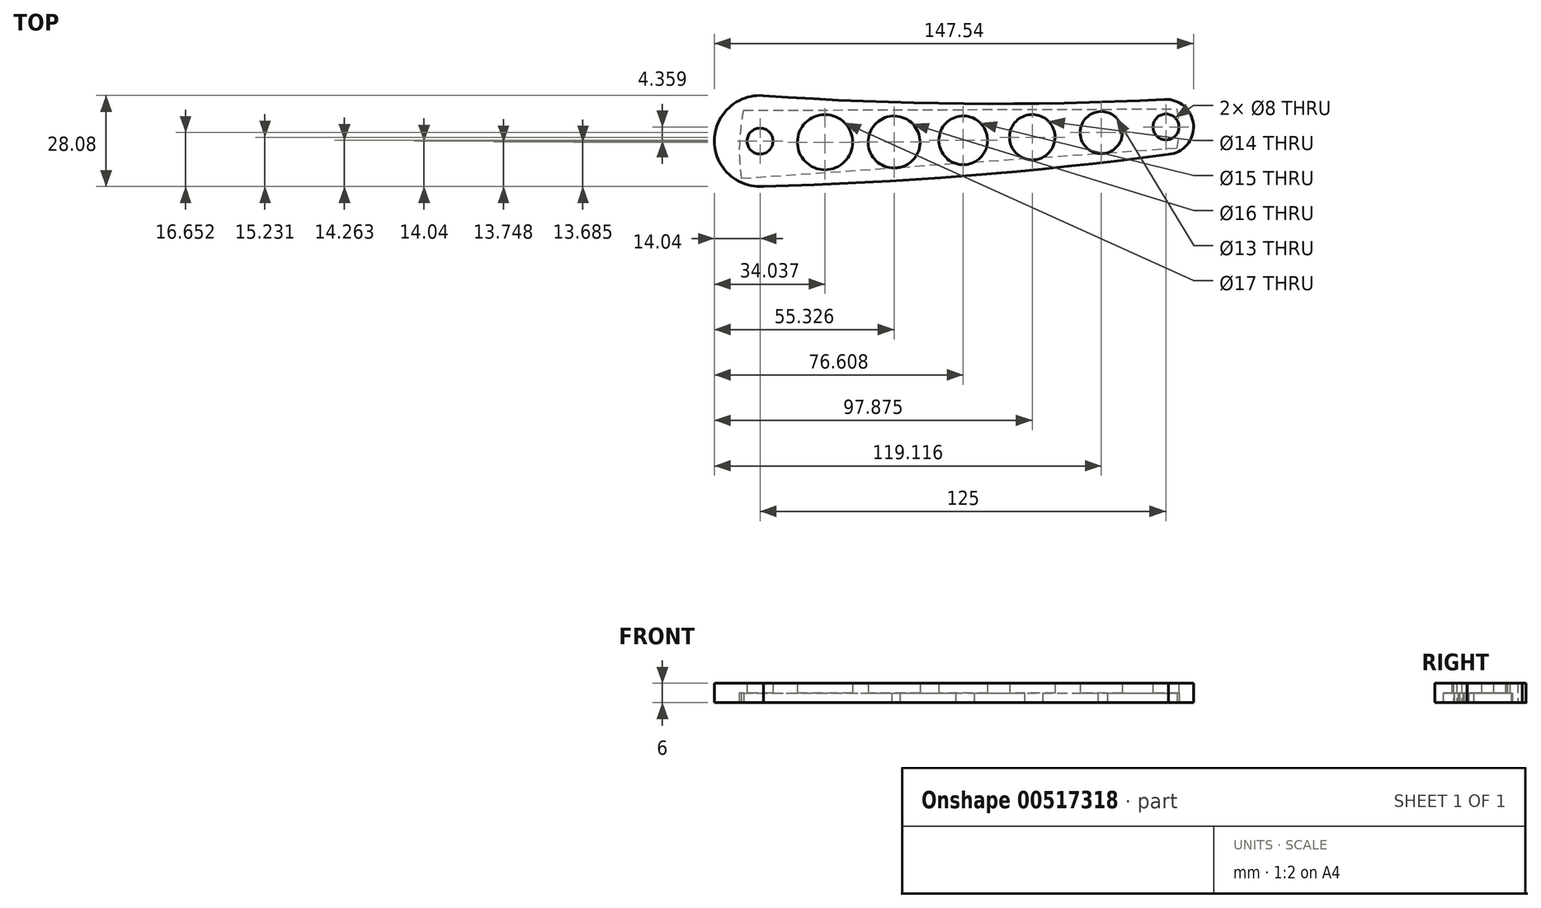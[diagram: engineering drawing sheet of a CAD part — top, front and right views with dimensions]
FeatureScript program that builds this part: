
annotation { "Feature Type Name" : "Feature", "Feature Type Description" : "" }
export const myFeature = defineFeature(function(context is Context, id is Id, definition is map)
    precondition{}
    {
        {
            var Q0;
            Q0=qCreatedBy(makeId("Top.planeOp"),FACE);
            var sketch = newSketch(context, id + "F0", { "sketchPlane" : qUnion([Q0])});
            skPoint(sketch, "E0", {"position": v(-80, 14) * mm});
            skPoint(sketch, "E1", {"position": v(45, 18.36) * mm});
            skArc(sketch, "E2", {"start": v(-79, 28) * mm, "mid": v(-17.24, 25.51) * mm, "end": v(44.55, 26.85) * mm});
            skArc(sketch, "E3", {"start": v(-80, 14) * mm, "mid": v(-17.43, 14.22) * mm, "end": v(45, 18.36) * mm, "construction": true});
            skArc(sketch, "E4", {"start": v(45.74, 9.9) * mm, "mid": v(53.48, 18.95) * mm, "end": v(44.55, 26.85) * mm});
            skArc(sketch, "E5", {"start": v(-79, 28) * mm, "mid": v(-94.04, 14) * mm, "end": v(-79, 0) * mm});
            skCircle(sketch, "E6", {"center": v(-80, 14) * mm, "radius": 4 * mm});
            skCircle(sketch, "E7", {"center": v(45, 18.36) * mm, "radius": 4 * mm});
            skCircle(sketch, "E8", {"center": v(-60, 13.65) * mm, "radius": 8.5 * mm});
            skCircle(sketch, "E9", {"center": v(-38.71, 13.7) * mm, "radius": 8 * mm});
            skCircle(sketch, "E10", {"center": v(-17.43, 14.22) * mm, "radius": 7.5 * mm});
            skCircle(sketch, "E11", {"center": v(3.84, 15.2) * mm, "radius": 7 * mm});
            skCircle(sketch, "E12", {"center": v(25.08, 16.61) * mm, "radius": 6.5 * mm});
            skLineSegment(sketch, "E13", {"start": v(-80, 14) * mm, "end": v(-60, 13.65) * mm, "construction": true});
            skLineSegment(sketch, "E14", {"start": v(-60, 13.65) * mm, "end": v(-38.71, 13.7) * mm, "construction": true});
            skLineSegment(sketch, "E15", {"start": v(-38.71, 13.7) * mm, "end": v(-17.43, 14.22) * mm, "construction": true});
            skLineSegment(sketch, "E16", {"start": v(-17.43, 14.22) * mm, "end": v(3.84, 15.2) * mm, "construction": true});
            skLineSegment(sketch, "E17", {"start": v(25.08, 16.61) * mm, "end": v(45, 18.36) * mm, "construction": true});
            skLineSegment(sketch, "E18", {"start": v(3.84, 15.2) * mm, "end": v(25.08, 16.61) * mm, "construction": true});
            skArc(sketch, "E19", {"start": v(-79, 0) * mm, "mid": v(-16.5, 3.3) * mm, "end": v(45.74, 9.9) * mm});
            skLineSegment(sketch, "E20", {"start": v(45, 18.36) * mm, "end": v(45.74, 9.9) * mm, "construction": true});
            skLineSegment(sketch, "E21", {"start": v(41.68, 9.36) * mm, "end": v(62.93, 12.1) * mm, "construction": true});
            skLineSegment(sketch, "E22", {"start": v(44.55, 26.85) * mm, "end": v(58.75, 27.6) * mm, "construction": true});
            skLineSegment(sketch, "E23", {"start": v(45, 18.36) * mm, "end": v(45, 64.58) * mm, "construction": true});
            skLineSegment(sketch, "E24", {"start": v(-79, 28) * mm, "end": v(-120.43, 30.95) * mm, "construction": true});
            skLineSegment(sketch, "E25", {"start": v(-73.81, 0.15) * mm, "end": v(-120.98, -1.31) * mm, "construction": true});
            skLineSegment(sketch, "E26", {"start": v(73.87, 0) * mm, "end": v(-126.58, 0) * mm, "construction": true});
            skSolve(sketch);
        }
        {
            var Q0;
            Q0 = qSketchRegion(id + "F0", true);
            extrude(context, id + "F1", {"entities" : qUnion([Q0]), "depth" : 6 * mm, "offsetDistance" : 25 * mm});
        }
        {
            var Q0;
            Q0=qCreatedBy(makeId("Top.planeOp"),FACE);
            var sketch = newSketch(context, id + "F2", { "sketchPlane" : qUnion([Q0])});
            skLineSegment(sketch, "E27", {"start": v(-85.1, 23.49) * mm, "end": v(48.4, 23.88) * mm});
            skLineSegment(sketch, "E28", {"start": v(48.4, 23.88) * mm, "end": v(48.44, 11.88) * mm, "construction": true});
            skLineSegment(sketch, "E29", {"start": v(-85.1, 23.49) * mm, "end": v(-85.77, 2.5) * mm, "construction": true});
            skLineSegment(sketch, "E30", {"start": v(-85.77, 2.5) * mm, "end": v(48.44, 11.88) * mm});
            skArc(sketch, "E31", {"start": v(48.44, 11.88) * mm, "mid": v(49.1, 17.89) * mm, "end": v(48.4, 23.88) * mm});
            skArc(sketch, "E32", {"start": v(-85.1, 23.49) * mm, "mid": v(-86.36, 13.02) * mm, "end": v(-85.77, 2.5) * mm});
            skLineSegment(sketch, "E33", {"start": v(45, -4.12) * mm, "end": v(45, 30.95) * mm, "construction": true});
            skLineSegment(sketch, "E34", {"start": v(-70.34, 2.5) * mm, "end": v(-85.77, 2.5) * mm, "construction": true});
            skPoint(sketch, "E35", {"position": v(45, 18.36) * mm});
            skLineSegment(sketch, "E36", {"start": v(-80, 14) * mm, "end": v(-85.1, 23.49) * mm, "construction": true});
            skLineSegment(sketch, "E37", {"start": v(-80, 14) * mm, "end": v(-91.7, 14.37) * mm, "construction": true});
            skLineSegment(sketch, "E38", {"start": v(-84, 14.13) * mm, "end": v(-84.8, -11.27) * mm, "construction": true});
            skLineSegment(sketch, "E39", {"start": v(-75.97, 14.93) * mm, "end": v(-75.2, 38.7) * mm, "construction": true});
            skSolve(sketch);
        }
        {
            var Q0;
            Q0 = qSketchRegion(id + "F2", true);
            extrude(context, id + "F3", {"entities" : qUnion([Q0]), "operationType" : NewBodyOperationType.REMOVE, "depth" : 3 * mm, "offsetDistance" : 25 * mm});
        }
    });
